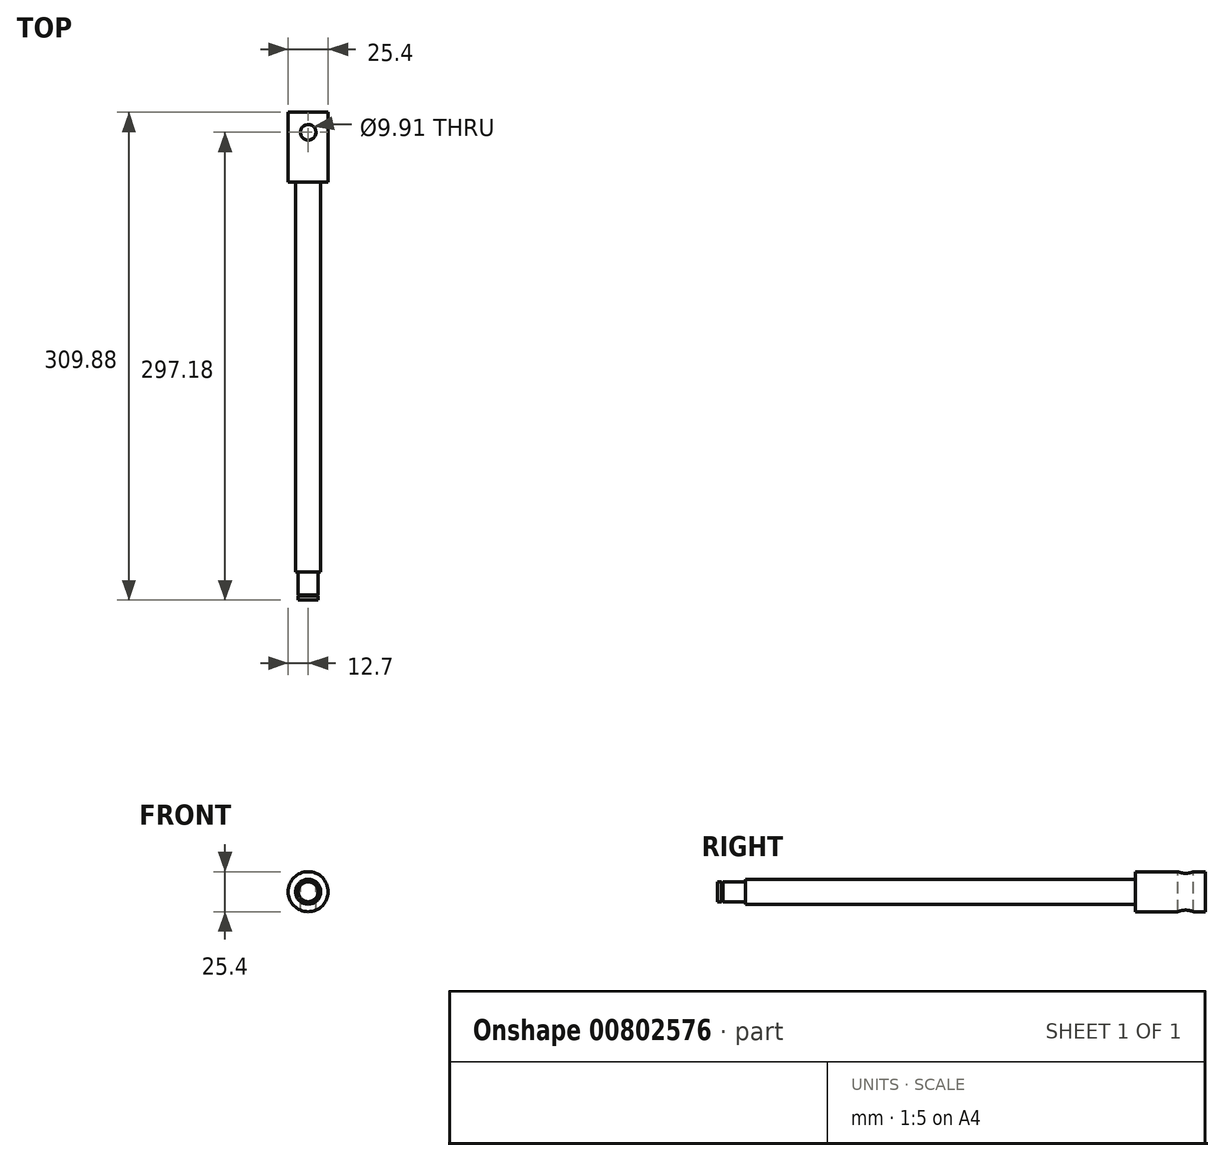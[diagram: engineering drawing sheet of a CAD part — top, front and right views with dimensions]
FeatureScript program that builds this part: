
annotation { "Feature Type Name" : "Feature", "Feature Type Description" : "" }
export const myFeature = defineFeature(function(context is Context, id is Id, definition is map)
    precondition{}
    {
        {
            var Q0;
            Q0=qCreatedBy(makeId("Front.planeOp"),FACE);
            var sketch = newSketch(context, id + "F0", { "sketchPlane" : qUnion([Q0])});
            skCircle(sketch, "E0", {"center": v(0, 0) * mm, "radius": 12.7 * mm});
            skSolve(sketch);
        }
        {
            var Q0;
            Q0=makeQuery(id+"F0.imprint","IMPRINT",FACE,{"disambiguationData":[TD([[makeQuery(id+"F0.imprint","IMPRINT",EDGE,{"derivedFrom":sQuery(id+"F0.wireOp",EDGE,"E0")}),1.0]])]});
            extrude(context, id + "F1", {"entities" : qUnion([Q0]), "oppositeDirection" : true, "depth" : 44.45 * mm, "offsetDistance" : 25.4 * mm});
        }
        {
            var Q0;
            Q0=makeQuery(id+"F1.opExtrude","CAP_FACE",FACE,{"disambiguationData":[OSD([sQuery(id+"F0.wireOp",EDGE,"E0")])],"isStart":true});
            var sketch = newSketch(context, id + "F2", { "sketchPlane" : qUnion([Q0])});
            skCircle(sketch, "E1", {"center": v(0, 0) * mm, "radius": 7.94 * mm});
            skSolve(sketch);
        }
        {
            var Q0;
            Q0=makeQuery(id+"F2.imprint","IMPRINT",FACE,{"disambiguationData":[TD([[makeQuery(id+"F2.imprint","IMPRINT",EDGE,{"derivedFrom":sQuery(id+"F2.wireOp",EDGE,"E1")}),1.0]])]});
            extrude(context, id + "F3", {"entities" : qUnion([Q0]), "operationType" : NewBodyOperationType.ADD, "depth" : 247.65 * mm, "offsetDistance" : 25.4 * mm});
        }
        {
            var Q0;
            Q0=makeQuery(id+"F3.opExtrude","CAP_FACE",FACE,{"disambiguationData":[OSD([sQuery(id+"F2.wireOp",EDGE,"E1")])],"isStart":false});
            var sketch = newSketch(context, id + "F4", { "sketchPlane" : qUnion([Q0])});
            skCircle(sketch, "E2", {"center": v(0, 0) * mm, "radius": 6.35 * mm});
            skSolve(sketch);
        }
        {
            var Q0;
            Q0=makeQuery(id+"F4.imprint","IMPRINT",FACE,{"disambiguationData":[TD([[makeQuery(id+"F4.imprint","IMPRINT",EDGE,{"derivedFrom":sQuery(id+"F4.wireOp",EDGE,"E2")}),1.0]])]});
            extrude(context, id + "F5", {"entities" : qUnion([Q0]), "operationType" : NewBodyOperationType.ADD, "depth" : 17.78 * mm, "offsetDistance" : 25.4 * mm});
        }
        {
            var Q0;
            Q0=qCreatedBy(makeId("Right.planeOp"),FACE);
            var sketch = newSketch(context, id + "F6", { "sketchPlane" : qUnion([Q0])});
            skLineSegment(sketch, "E3", {"start": v(-262.9, 7.3) * mm, "end": v(-262.9, -10.46) * mm, "construction": true});
            skLineSegment(sketch, "E4", {"start": v(-262.9, 7.3) * mm, "end": v(-262.9, 5.75) * mm});
            skLineSegment(sketch, "E5", {"start": v(-262.9, 5.75) * mm, "end": v(-262.03, 5.75) * mm});
            skLineSegment(sketch, "E6", {"start": v(-262.03, 5.75) * mm, "end": v(-262.03, 7.23) * mm});
            skLineSegment(sketch, "E7", {"start": v(-262.03, 7.23) * mm, "end": v(-262.9, 7.23) * mm});
            skLineSegment(sketch, "E8", {"start": v(-266.62, 0) * mm, "end": v(-254.34, 0) * mm, "construction": true});
            skSolve(sketch);
        }
        {
            var Q0;
            {var subQ0=sQuery(id+"F6.wireOp",EDGE,"E5");Q0=makeQuery(id+"F6.imprint","IMPRINT",FACE,{"disambiguationData":[TD([[makeQuery(id+"F6.imprint","IMPRINT",EDGE,{"derivedFrom":subQ0}),1.0]])]});}
            var Q1;
            Q1=sQuery(id+"F6.wireOp",EDGE,"E8");
            revolve(context, id + "F7", {"operationType" : NewBodyOperationType.REMOVE, "surfaceOperationType" : NewSurfaceOperationType.NEW, "entities" : qUnion([Q0]), "axis" : qUnion([Q1]), "revolveType" : RevolveType.FULL, "oppositeDirection" : true});
        }
        {
            var Q0;
            Q0=qCreatedBy(makeId("Top.planeOp"),FACE);
            var sketch = newSketch(context, id + "F8", { "sketchPlane" : qUnion([Q0])});
            skCircle(sketch, "E9", {"center": v(0, 31.75) * mm, "radius": 4.95 * mm});
            skSolve(sketch);
        }
        {
            var Q0;
            Q0=makeQuery(id+"F8.imprint","IMPRINT",FACE,{"disambiguationData":[TD([[makeQuery(id+"F8.imprint","IMPRINT",EDGE,{"derivedFrom":sQuery(id+"F8.wireOp",EDGE,"E9")}),1.0]])]});
            extrude(context, id + "F9", {"entities" : qUnion([Q0]), "operationType" : NewBodyOperationType.REMOVE, "oppositeDirection" : true, "depth" : 25.4 * mm, "offsetDistance" : 25.4 * mm, "hasSecondDirection" : true, "secondDirectionOppositeDirection" : false, "secondDirectionDepth" : 25.4 * mm});
        }
    });
